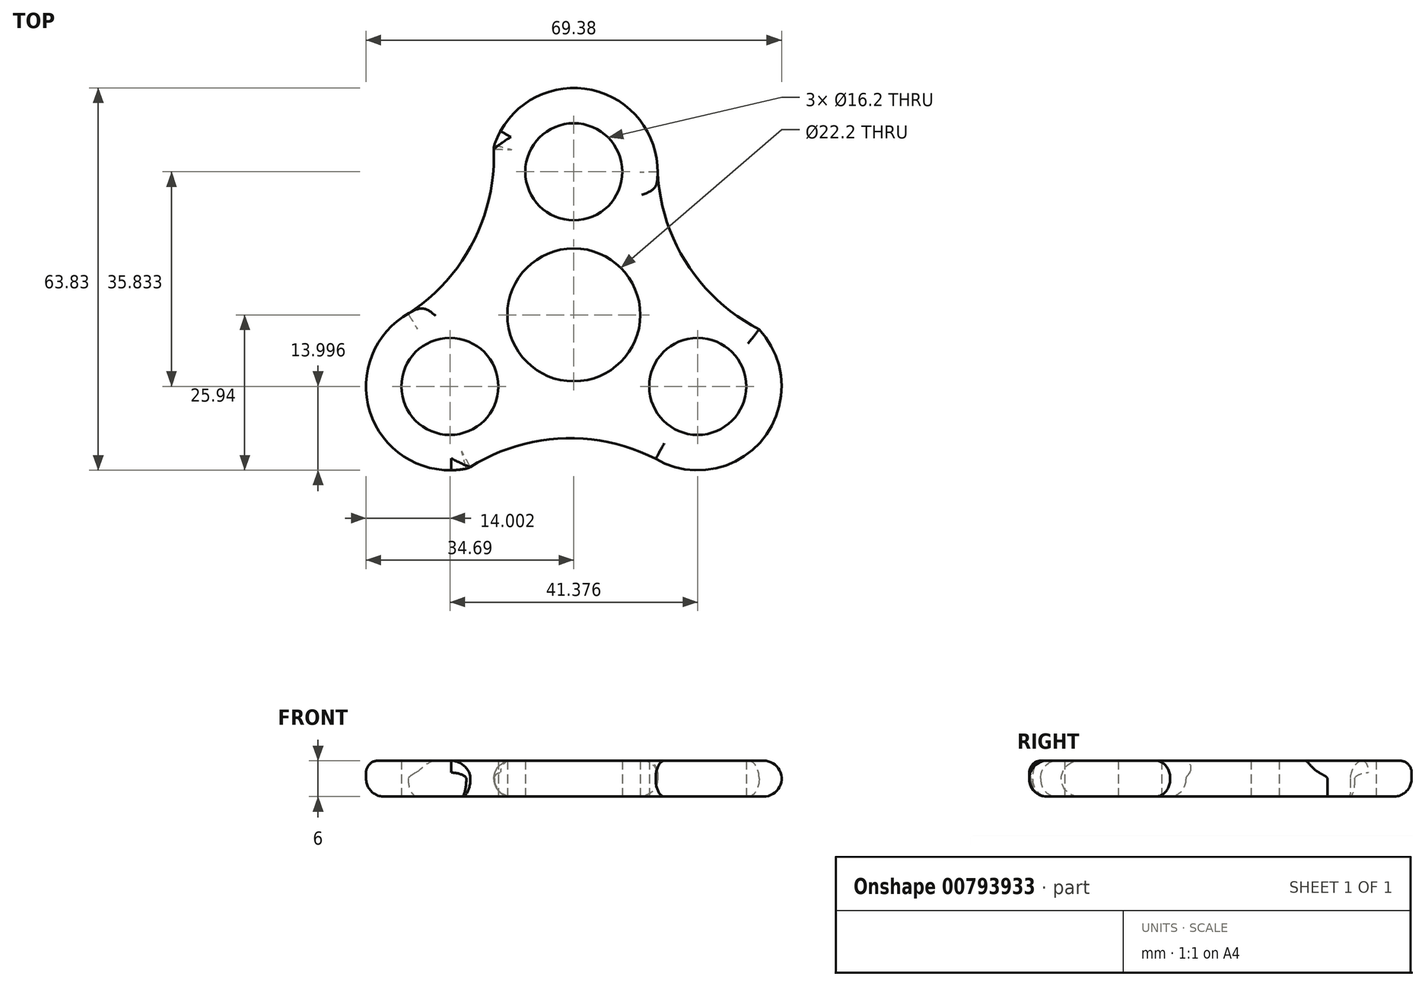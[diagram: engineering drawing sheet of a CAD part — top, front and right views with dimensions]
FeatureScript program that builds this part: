
annotation { "Feature Type Name" : "Feature", "Feature Type Description" : "" }
export const myFeature = defineFeature(function(context is Context, id is Id, definition is map)
    precondition{}
    {
        {
            var Q0;
            Q0=qCreatedBy(makeId("Top.planeOp"),FACE);
            var sketch = newSketch(context, id + "F0", { "sketchPlane" : qUnion([Q0])});
            skCircle(sketch, "E0", {"center": v(0, 0) * mm, "radius": 11.1 * mm});
            skCircle(sketch, "E1", {"center": v(0, 0) * mm, "radius": 3.75 * mm});
            skCircle(sketch, "E2", {"center": v(0, 23.89) * mm, "radius": 8.1 * mm});
            skCircle(sketch, "E3", {"center": v(0, 23.89) * mm, "radius": 3.75 * mm});
            skCircle(sketch, "E4.1.0", {"center": v(-20.69, -11.94) * mm, "radius": 3.75 * mm});
            skCircle(sketch, "E4.1.1", {"center": v(-20.69, -11.94) * mm, "radius": 8.1 * mm});
            skCircle(sketch, "E4.2.0", {"center": v(20.69, -11.94) * mm, "radius": 3.75 * mm});
            skCircle(sketch, "E4.2.1", {"center": v(20.69, -11.94) * mm, "radius": 8.1 * mm});
            skLineSegment(sketch, "E5", {"start": v(-21.01, 24.56) * mm, "end": v(-21.01, 24.56) * mm});
            skArc(sketch, "E6", {"start": v(14, 23.86) * mm, "mid": v(2.1, 37.73) * mm, "end": v(-13.38, 28) * mm});
            skArc(sketch, "E7.1.0", {"start": v(-27.66, 0.2) * mm, "mid": v(-33.72, -17.05) * mm, "end": v(-17.56, -25.6) * mm});
            skArc(sketch, "E7.2.0", {"start": v(13.66, -24.05) * mm, "mid": v(31.63, -20.68) * mm, "end": v(30.94, -2.41) * mm});
            skArc(sketch, "E8", {"start": v(-27.66, 0.2) * mm, "mid": v(-16.79, 12.18) * mm, "end": v(-13.38, 28) * mm});
            skArc(sketch, "E9.1.0", {"start": v(13.66, -24.05) * mm, "mid": v(-2.16, -20.63) * mm, "end": v(-17.56, -25.6) * mm});
            skArc(sketch, "E9.2.0", {"start": v(14, 23.86) * mm, "mid": v(18.94, 8.45) * mm, "end": v(30.94, -2.41) * mm});
            skSolve(sketch);
        }
        {
            var Q0;
            Q0=makeQuery(id+"F0.imprint","IMPRINT",FACE,{"disambiguationData":[TD([[makeQuery(id+"F0.imprint","IMPRINT",EDGE,{"derivedFrom":sQuery(id+"F0.wireOp",EDGE,"E0")}),-1.0]])]});
            extrude(context, id + "F1", {"entities" : qUnion([Q0]), "depth" : 6 * mm, "offsetDistance" : 25 * mm});
        }
        {
            var Q0;
            Q0=makeQuery(id+"F1.opExtrude","CAP_EDGE",EDGE,{"disambiguationData":[OSD([sQuery(id+"F0.wireOp",EDGE,"E9.2.0")])],"isStart":true});
            var Q1;
            Q1=makeQuery(id+"F1.opExtrude","CAP_EDGE",EDGE,{"disambiguationData":[OSD([sQuery(id+"F0.wireOp",EDGE,"E7.2.0")])],"isStart":true});
            var Q2;
            Q2=makeQuery(id+"F1.opExtrude","CAP_EDGE",EDGE,{"disambiguationData":[OSD([sQuery(id+"F0.wireOp",EDGE,"E7.1.0")])],"isStart":true});
            var Q3;
            Q3=makeQuery(id+"F1.opExtrude","CAP_EDGE",EDGE,{"disambiguationData":[OSD([sQuery(id+"F0.wireOp",EDGE,"E6")])],"isStart":true});
            var Q4;
            Q4=makeQuery(id+"F1.opExtrude","CAP_EDGE",EDGE,{"disambiguationData":[OSD([sQuery(id+"F0.wireOp",EDGE,"E9.2.0")])],"isStart":false});
            var Q5;
            Q5=makeQuery(id+"F1.opExtrude","CAP_EDGE",EDGE,{"disambiguationData":[OSD([sQuery(id+"F0.wireOp",EDGE,"E7.2.0")])],"isStart":false});
            var Q6;
            Q6=makeQuery(id+"F1.opExtrude","CAP_EDGE",EDGE,{"disambiguationData":[OSD([sQuery(id+"F0.wireOp",EDGE,"E8")])],"isStart":false});
            fillet(context, id + "F2", {"entities" : qUnion([Q0, Q1, Q2, Q3, Q4, Q5, Q6]), "radius" : 3 * mm, "tangentPropagation" : true, "allowEdgeOverflow" : false});
        }
        {
            var Q0;
            Q0=makeQuery(id+"F1.opExtrude","CAP_EDGE",EDGE,{"disambiguationData":[OSD([sQuery(id+"F0.wireOp",EDGE,"E7.1.0")])],"isStart":false});
            var Q1;
            Q1=makeQuery(id+"F1.opExtrude","CAP_EDGE",EDGE,{"disambiguationData":[OSD([sQuery(id+"F0.wireOp",EDGE,"E6")])],"isStart":false});
            fillet(context, id + "F3", {"entities" : qUnion([Q0, Q1]), "radius" : 2 * mm, "tangentPropagation" : true, "allowEdgeOverflow" : false});
        }
    });
